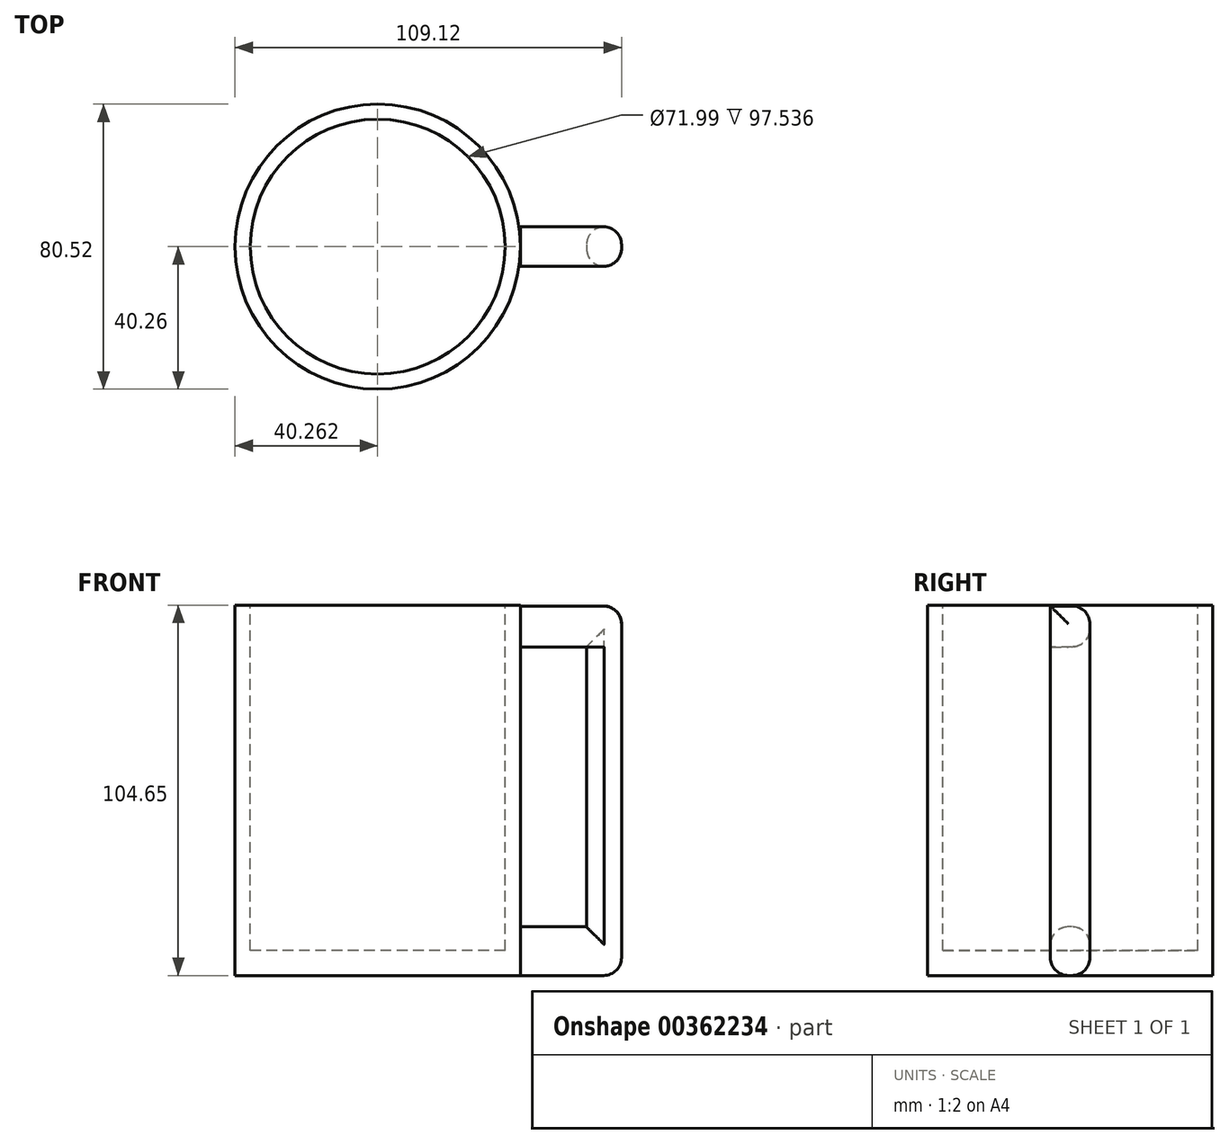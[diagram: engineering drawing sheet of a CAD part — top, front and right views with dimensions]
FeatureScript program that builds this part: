
annotation { "Feature Type Name" : "Feature", "Feature Type Description" : "" }
export const myFeature = defineFeature(function(context is Context, id is Id, definition is map)
    precondition{}
    {
        {
            var Q0;
            Q0=qCreatedBy(makeId("Top.planeOp"),FACE);
            var sketch = newSketch(context, id + "F0", { "sketchPlane" : qUnion([Q0])});
            skCircle(sketch, "E0", {"center": v(-39.67, 0) * mm, "radius": 40.26 * mm});
            skSolve(sketch);
        }
        {
            var Q0;
            Q0 = qSketchRegion(id + "F0", true);
            extrude(context, id + "F1", {"entities" : qUnion([Q0]), "depth" : 104.65 * mm});
        }
        {
            var Q0;
            Q0=makeQuery(id+"F1.opExtrude","CAP_FACE",FACE,{"disambiguationData":[OSD([sQuery(id+"F0.wireOp",EDGE,"E0")])],"isStart":false});
            var sketch = newSketch(context, id + "F2", { "sketchPlane" : qUnion([Q0])});
            skCircle(sketch, "E1", {"center": v(-39.67, 0) * mm, "radius": 36 * mm});
            skSolve(sketch);
        }
        {
            var Q0;
            Q0 = qSketchRegion(id + "F2", true);
            extrude(context, id + "F3", {"entities" : qUnion([Q0]), "operationType" : NewBodyOperationType.REMOVE, "oppositeDirection" : true, "depth" : 97.54 * mm});
        }
        {
            var Q0;
            Q0=qCreatedBy(makeId("Front.planeOp"),FACE);
            var sketch = newSketch(context, id + "F4", { "sketchPlane" : qUnion([Q0])});
            skLineSegment(sketch, "E2.bottom", {"start": v(0.63, 0) * mm, "end": v(29.19, 0) * mm});
            skLineSegment(sketch, "E2.top", {"start": v(0.63, 104.38) * mm, "end": v(29.19, 104.38) * mm});
            skLineSegment(sketch, "E2.left", {"start": v(0.63, 0) * mm, "end": v(0.63, 104.38) * mm});
            skLineSegment(sketch, "E2.right", {"start": v(29.19, 0) * mm, "end": v(29.19, 104.38) * mm});
            skLineSegment(sketch, "E3.bottom", {"start": v(0.63, 13.75) * mm, "end": v(19.3, 13.75) * mm});
            skLineSegment(sketch, "E3.top", {"start": v(0.63, 92.85) * mm, "end": v(19.3, 92.85) * mm});
            skLineSegment(sketch, "E3.left", {"start": v(0.63, 13.75) * mm, "end": v(0.63, 92.85) * mm});
            skLineSegment(sketch, "E3.right", {"start": v(19.3, 13.75) * mm, "end": v(19.3, 92.85) * mm});
            skSolve(sketch);
        }
        {
            var Q0;
            Q0 = qSketchRegion(id + "F4", true);
            extrude(context, id + "F5", {"entities" : qUnion([Q0]), "depth" : 5.6 * mm});
        }
        {
            var Q0;
            {var subQ4=sQuery(id+"F4.wireOp",EDGE,"E2.bottom");Q0=makeQuery(id+"F4.imprint","IMPRINT",FACE,{"disambiguationData":[TD([[makeQuery(id+"F4.imprint","IMPRINT",EDGE,{"derivedFrom":subQ4}),1.0]])]});}
            extrude(context, id + "F6", {"entities" : qUnion([Q0]), "operationType" : NewBodyOperationType.ADD, "oppositeDirection" : true, "depth" : 5.6 * mm});
        }
        {
            var Q0;
            Q0=makeQuery(id+"F4.imprint","IMPRINT",FACE,{"disambiguationData":[TD([[makeQuery(id+"F4.imprint","IMPRINT",EDGE,{"derivedFrom":sQuery(id+"F4.wireOp",EDGE,"E3.bottom")}),1.0]])]});
            extrude(context, id + "F7", {"entities" : qUnion([Q0]), "operationType" : NewBodyOperationType.REMOVE, "depth" : 72.39 * mm});
        }
        {
            var Q0;
            {var subQ0=sQuery(id+"F4.wireOp",EDGE,"E2.right");var subQ1=sQuery(id+"F4.wireOp",EDGE,"E2.top");Q0=makeQuery(id+"F6.boolean.opBoolean","MERGE",EDGE,{"derivedFrom":[makeQuery(id+"F5.opExtrude","SWEPT_EDGE",EDGE,{"disambiguationData":[OSD([subQ1,subQ0])]}),makeQuery(id+"F6.opExtrude","SWEPT_EDGE",EDGE,{"disambiguationData":[OSD([subQ1,subQ0])]})]});}
            var Q1;
            {var subQ0=sQuery(id+"F4.wireOp",EDGE,"E2.right");var subQ1=sQuery(id+"F4.wireOp",EDGE,"E2.bottom");Q1=makeQuery(id+"F6.boolean.opBoolean","MERGE",EDGE,{"derivedFrom":[makeQuery(id+"F5.opExtrude","SWEPT_EDGE",EDGE,{"disambiguationData":[OSD([subQ1,subQ0])]}),makeQuery(id+"F6.opExtrude","SWEPT_EDGE",EDGE,{"disambiguationData":[OSD([subQ1,subQ0])]})]});}
            var Q2;
            Q2=makeQuery(id+"F7.boolean.opBoolean","INTERSECT",EDGE,{"derivedFrom":[makeQuery(id+"F5.opExtrude","CAP_FACE",FACE,{"disambiguationData":[OSD([sQuery(id+"F4.wireOp",EDGE,"E2.bottom"),sQuery(id+"F4.wireOp",EDGE,"E2.top"),sQuery(id+"F4.wireOp",EDGE,"E2.left"),sQuery(id+"F4.wireOp",EDGE,"E2.right"),sQuery(id+"F4.wireOp",EDGE,"E3.left")])],"isStart":false}),makeQuery(id+"F7.opExtrude","SWEPT_FACE",FACE,{"disambiguationData":[OSD([sQuery(id+"F4.wireOp",EDGE,"E3.bottom")])]})]});
            var Q3;
            Q3=makeQuery(id+"F7.boolean.opBoolean","INTERSECT",EDGE,{"derivedFrom":[makeQuery(id+"F5.opExtrude","CAP_FACE",FACE,{"disambiguationData":[OSD([sQuery(id+"F4.wireOp",EDGE,"E2.bottom"),sQuery(id+"F4.wireOp",EDGE,"E2.top"),sQuery(id+"F4.wireOp",EDGE,"E2.left"),sQuery(id+"F4.wireOp",EDGE,"E2.right"),sQuery(id+"F4.wireOp",EDGE,"E3.left")])],"isStart":false}),makeQuery(id+"F7.opExtrude","SWEPT_FACE",FACE,{"disambiguationData":[OSD([sQuery(id+"F4.wireOp",EDGE,"E3.right")])]})]});
            var Q4;
            Q4=makeQuery(id+"F5.opExtrude","CAP_EDGE",EDGE,{"disambiguationData":[OSD([sQuery(id+"F4.wireOp",EDGE,"E2.right")])],"isStart":false});
            var Q5;
            Q5=makeQuery(id+"F6.opExtrude","CAP_EDGE",EDGE,{"disambiguationData":[OSD([sQuery(id+"F4.wireOp",EDGE,"E2.right")])],"isStart":false});
            var Q6;
            Q6=makeQuery(id+"F6.opExtrude","CAP_EDGE",EDGE,{"disambiguationData":[OSD([sQuery(id+"F4.wireOp",EDGE,"E2.top")])],"isStart":false});
            var Q7;
            Q7=makeQuery(id+"F6.opExtrude","CAP_EDGE",EDGE,{"disambiguationData":[OSD([sQuery(id+"F4.wireOp",EDGE,"E3.top")])],"isStart":false});
            var Q8;
            Q8=makeQuery(id+"F6.opExtrude","CAP_EDGE",EDGE,{"disambiguationData":[OSD([sQuery(id+"F4.wireOp",EDGE,"E3.right")])],"isStart":false});
            var Q9;
            Q9=makeQuery(id+"F6.opExtrude","CAP_EDGE",EDGE,{"disambiguationData":[OSD([sQuery(id+"F4.wireOp",EDGE,"E3.bottom")])],"isStart":false});
            var Q10;
            Q10=makeQuery(id+"F6.opExtrude","CAP_EDGE",EDGE,{"disambiguationData":[OSD([sQuery(id+"F4.wireOp",EDGE,"E2.bottom")])],"isStart":false});
            var Q11;
            Q11=makeQuery(id+"F5.opExtrude","CAP_EDGE",EDGE,{"disambiguationData":[OSD([sQuery(id+"F4.wireOp",EDGE,"E2.bottom")])],"isStart":false});
            fillet(context, id + "F8", {"entities" : qUnion([Q0, Q1, Q2, Q3, Q4, Q5, Q6, Q7, Q8, Q9, Q10, Q11]), "radius" : 5.08 * mm, "tangentPropagation" : true, "allowEdgeOverflow" : false});
        }
    });
